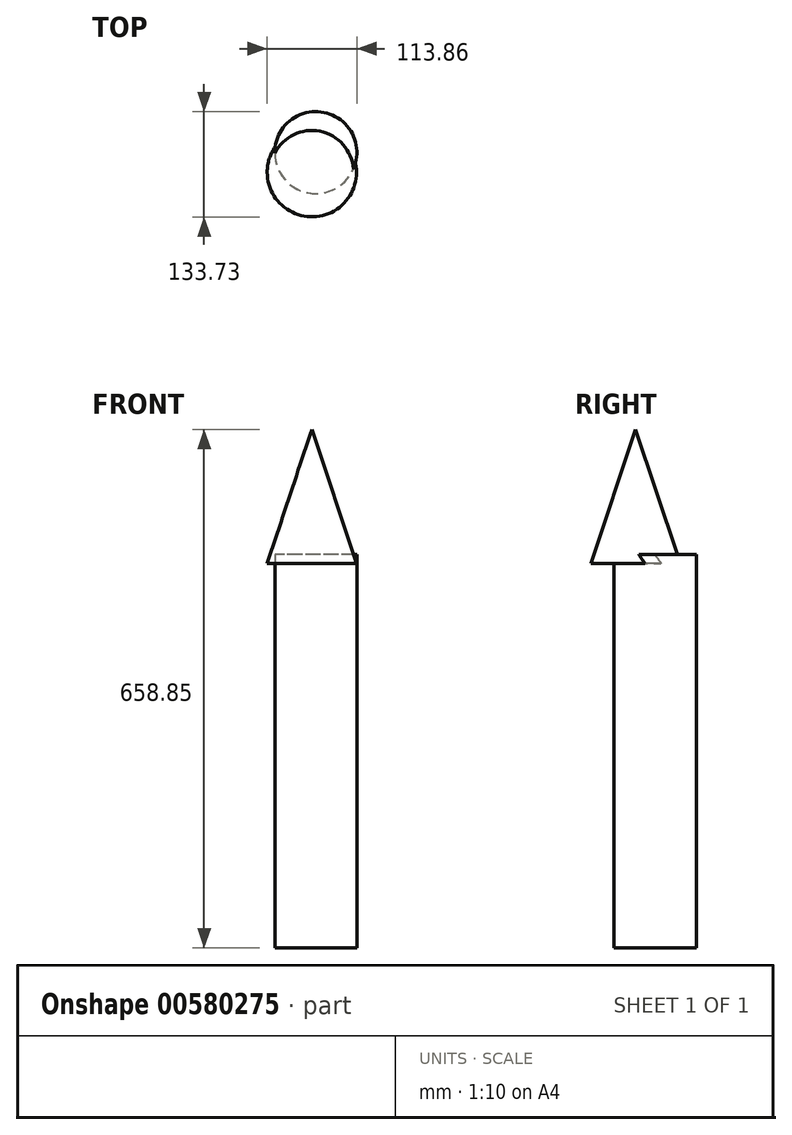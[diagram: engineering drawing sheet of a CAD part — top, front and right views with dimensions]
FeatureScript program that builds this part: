
annotation { "Feature Type Name" : "Feature", "Feature Type Description" : "" }
export const myFeature = defineFeature(function(context is Context, id is Id, definition is map)
    precondition{}
    {
        {
            var Q0;
            Q0=qCreatedBy(makeId("Top.planeOp"),FACE);
            var sketch = newSketch(context, id + "F0", { "sketchPlane" : qUnion([Q0])});
            skCircle(sketch, "E0", {"center": v(-29.71, 24.9) * mm, "radius": 52.1 * mm});
            skSolve(sketch);
        }
        {
            var Q0;
            Q0 = qSketchRegion(id + "F0", true);
            extrude(context, id + "F1", {"entities" : qUnion([Q0]), "depth" : 500 * mm, "offsetDistance" : 25 * mm});
        }
        {
            var Q0;
            Q0=qCreatedBy(makeId("Front.planeOp"),FACE);
            var sketch = newSketch(context, id + "F2", { "sketchPlane" : qUnion([Q0])});
            skLineSegment(sketch, "E1", {"start": v(-34.75, 488.63) * mm, "end": v(-34.75, 658.85) * mm});
            skLineSegment(sketch, "E2", {"start": v(-34.75, 658.85) * mm, "end": v(-91.47, 488.63) * mm});
            skLineSegment(sketch, "E3", {"start": v(-91.47, 488.63) * mm, "end": v(-34.75, 488.63) * mm});
            skSolve(sketch);
        }
        {
            var Q0;
            Q0=makeQuery(id+"F2.imprint","IMPRINT",FACE,{"disambiguationData":[TD([[makeQuery(id+"F2.imprint","IMPRINT",EDGE,{"derivedFrom":sQuery(id+"F2.wireOp",EDGE,"E1")}),1.0]])]});
            var Q1;
            Q1=sQuery(id+"F2.wireOp",EDGE,"E1");
            revolve(context, id + "F3", {"operationType" : NewBodyOperationType.ADD, "entities" : qUnion([Q0]), "axis" : qUnion([Q1]), "revolveType" : RevolveType.FULL});
        }
    });
